# Revit family: LTRI
name_source: partatom
category: Lighting Fixtures
units: mm (PartAtom-declared; Revit-internal decimal feet)

## family parameters
Always vertical = Yes
Cut with Voids When Loaded = No
Host = Wall
Light Source = Yes
OmniClass Number = 23.80.70.11.14
OmniClass Title = General Luminaries, Directional
Part Type = Normal
Room Calculation Point = No
Round Connector Dimension = Use Diameter
Shared = No

## types (5) — shared parameters
Assembly Code = D5020200
Color Filter = 16777215
Description = ADA Surface Mount LED Luminaire
Dimming Lamp Color Temperature Shift = <None>
Housing Finish = Metal - Viscor - White
Lamp = LED
Lens Finish = Polycarbonate - Viscor -  Soft Matte White Opal
Manufacturer = VISIONEERING by VISCOR
Model = LTRI
Tilt Angle = 180.00°
URL = https://www.viscor.com
Voltage = 120 V

## per-type parameters (varying)
| type | Apparent Load | Emit from Line Length | Lamp Wattage | Length | Photometric Web File |
| LTRI24-LED840K010LUNV | 8 VA | 1' - 11 1/16" | 8 VA | 1' - 11 1/16" | LTRI24-LED840K010LUNV-G002212.IES |
| LTRI48-LED840K018LUNV | 13 VA | 3' - 9 1/16" | 13 VA | 3' - 9 1/16" | LTRI48-LED840K018LUNV-G002217.IES |
| LTRI24-LED840K016LUNV | 15 VA | 1' - 11 1/16" | 15 VA | 1' - 11 1/16" | LTRI24-LED840K016LUNV-G002214.IES |
| LTRI48-LED840K037LUNV | 29 VA | 3' - 9 1/16" | 29 VA | 3' - 9 1/16" | LTRI48-LED840K037LUNV-G002229.IES |
| LTRI48-LED840K050LUNV | 34 VA | 3' - 9 1/16" | 34 VA | 3' - 9 1/16" | LTRI48-LED840K050LUNV-G002231.IES |

## geometry (parser evidence)
native form markers: Sweep x3
no freeform markers — native parametric forms only
